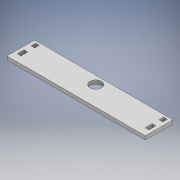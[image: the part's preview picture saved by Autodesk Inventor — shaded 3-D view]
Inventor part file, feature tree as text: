
AUTODESK INVENTOR PART (.ipt)
format: ipt  version: 2018.3 (Build 223284000, 284)  size: 124,928 bytes
history: native  units: mm
features: extrude x2, sketch x2
ambient origin geometry x8: Origin, YZ Plane, XZ Plane, XY Plane, X Axis, Y Axis, Z Axis, Center Point
bodies: Solid1 (feature_tree)
feature tree (4):
  extrude  "Extrusion1"  Depth=10.0mm
  extrude  "Extrusion2"  Depth=1.5875mm
  sketch  "Sketch1"  dims[d0=54.0mm d1=10.0mm]
  sketch  "Sketch2"  dims[d2=2.0mm d3=1.5875mm d4=3.0mm d5=1.5875mm d6=3.0mm d7=60.0mm d8=12.0mm d9=1.5875mm d10=0.0mm d11=5.0mm d12=1.5875mm d13=0.0mm]
